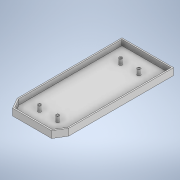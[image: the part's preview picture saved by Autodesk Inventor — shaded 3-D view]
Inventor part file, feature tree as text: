
AUTODESK INVENTOR PART (.ipt)
format: ipt  version: 2022 (Build 260153000, 153)  size: 211,968 bytes
history: native  units: in
note: dims shown in document units (in); Inventor stores cm internally (conversion verified against a paired STEP export)
features: extrude x4, projected_geometry x4, sketch x3
ambient origin geometry x8: Origin, YZ Plane, XZ Plane, XY Plane, X Axis, Y Axis, Z Axis, Center Point
bodies: Solid1 (feature_tree)
feature tree (11):
  sketch  "Sketch1"  dims[d0=0.003in d1=0.0625in]
  extrude  "Extrusion1"  Depth=0.0625in
  extrude  "Extrusion2"  Depth=0.0625in TaperAngle=0.0deg
  extrude  "Extrusion3"  Depth=0.0625in TaperAngle=0.0deg
  extrude  "Extrusion4"  Depth=0.0625in
  sketch  "Sketch2"  dims[d2=0.25in d3=0.0in d4=0.0625in d5=0.0in]
  projected_geometry  "Projected Loop1"
  sketch  "Sketch3"  dims[d6=0.15in d7=0.0625in d8=0.0in d9=0.1in d10=0.1in d11=0.0in]
  projected_geometry  "Projected Loop2"
  projected_geometry  "Projected Loop3"
  projected_geometry  "Projected Loop4"
